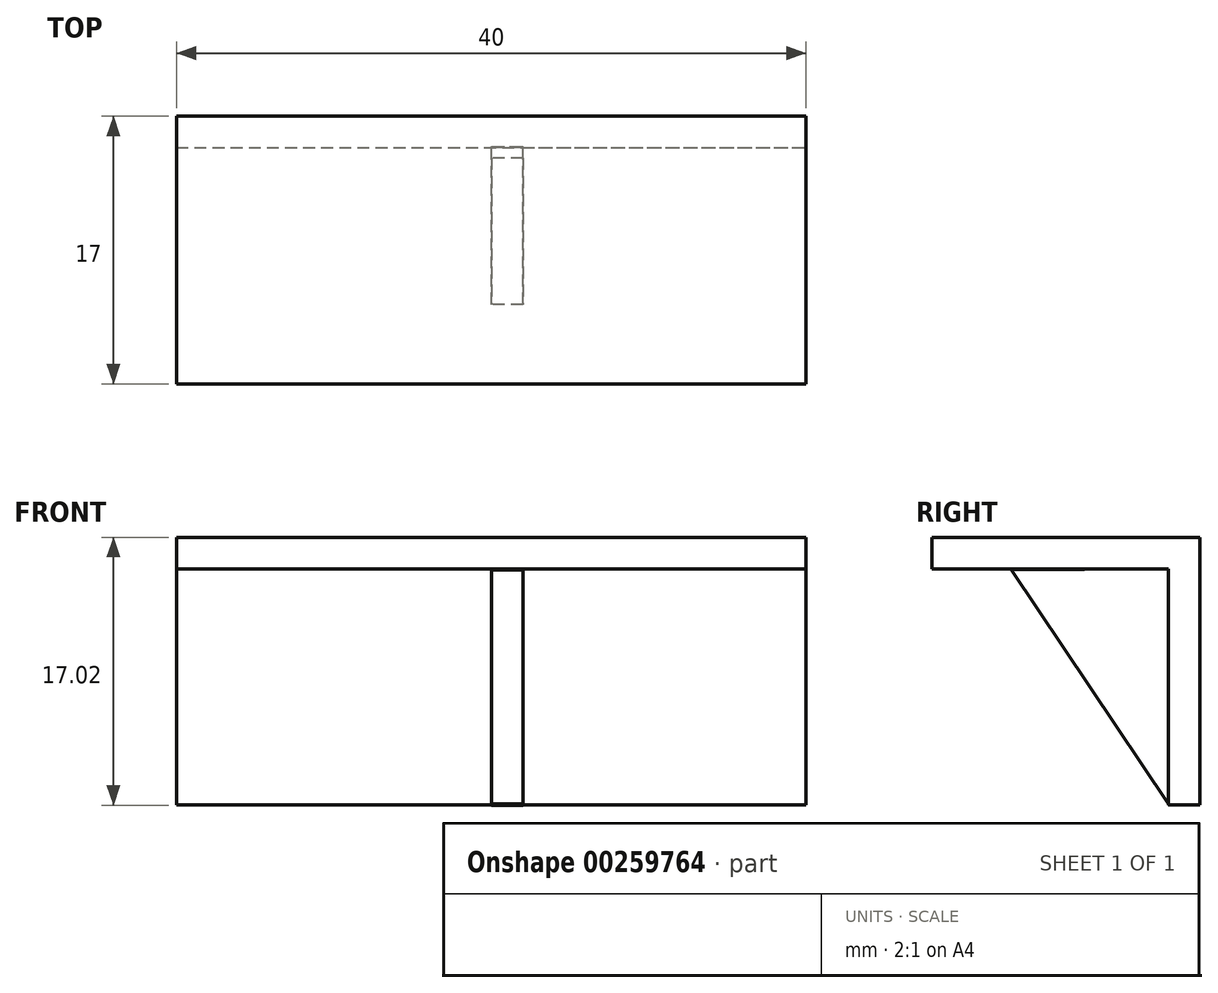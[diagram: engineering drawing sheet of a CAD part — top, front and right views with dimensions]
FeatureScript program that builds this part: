
annotation { "Feature Type Name" : "Feature", "Feature Type Description" : "" }
export const myFeature = defineFeature(function(context is Context, id is Id, definition is map)
    precondition{}
    {
        {
            var Q0;
            Q0=qCreatedBy(makeId("Front.planeOp"),FACE);
            var sketch = newSketch(context, id + "F0", { "sketchPlane" : qUnion([Q0])});
            skLineSegment(sketch, "E0.bottom", {"start": v(-20, 8.5) * mm, "end": v(20, 8.5) * mm});
            skLineSegment(sketch, "E0.top", {"start": v(-20, -8.5) * mm, "end": v(20, -8.5) * mm});
            skLineSegment(sketch, "E0.left", {"start": v(-20, 8.5) * mm, "end": v(-20, -8.5) * mm});
            skLineSegment(sketch, "E0.right", {"start": v(20, 8.5) * mm, "end": v(20, -8.5) * mm});
            skPoint(sketch, "E0.middle", {"position": v(0, 0) * mm});
            skSolve(sketch);
        }
        {
            var Q0;
            Q0 = qSketchRegion(id + "F0", true);
            extrude(context, id + "F1", {"entities" : qUnion([Q0]), "depth" : 2 * mm});
        }
        {
            var Q0;
            Q0=makeQuery(id+"F1.opExtrude","CAP_FACE",FACE,{"disambiguationData":[OSD([sQuery(id+"F0.wireOp",EDGE,"E0.bottom"),sQuery(id+"F0.wireOp",EDGE,"E0.top"),sQuery(id+"F0.wireOp",EDGE,"E0.left"),sQuery(id+"F0.wireOp",EDGE,"E0.right")])],"isStart":false});
            var sketch = newSketch(context, id + "F2", { "sketchPlane" : qUnion([Q0])});
            skLineSegment(sketch, "E1.bottom", {"start": v(-20, 8.5) * mm, "end": v(20, 8.5) * mm});
            skLineSegment(sketch, "E1.top", {"start": v(-20, 6.5) * mm, "end": v(20, 6.5) * mm});
            skLineSegment(sketch, "E1.left", {"start": v(-20, 8.5) * mm, "end": v(-20, 6.5) * mm});
            skLineSegment(sketch, "E1.right", {"start": v(20, 8.5) * mm, "end": v(20, 6.5) * mm});
            skSolve(sketch);
        }
        {
            var Q0;
            Q0 = qSketchRegion(id + "F2", true);
            extrude(context, id + "F3", {"entities" : qUnion([Q0]), "operationType" : NewBodyOperationType.ADD, "depth" : 15 * mm});
        }
        {
            var Q0;
            Q0=qCreatedBy(makeId("Right.planeOp"),FACE);
            var sketch = newSketch(context, id + "F4", { "sketchPlane" : qUnion([Q0])});
            skLineSegment(sketch, "E2", {"start": v(-11.96, 6.44) * mm, "end": v(-1.94, -8.52) * mm});
            skLineSegment(sketch, "E3", {"start": v(-1.94, -8.52) * mm, "end": v(-1.94, 6.5) * mm});
            skLineSegment(sketch, "E4", {"start": v(-1.94, 6.5) * mm, "end": v(-11.96, 6.44) * mm});
            skSolve(sketch);
        }
        {
            var Q0;
            Q0 = qSketchRegion(id + "F4", true);
            extrude(context, id + "F5", {"entities" : qUnion([Q0]), "operationType" : NewBodyOperationType.ADD, "depth" : 2 * mm});
        }
    });
